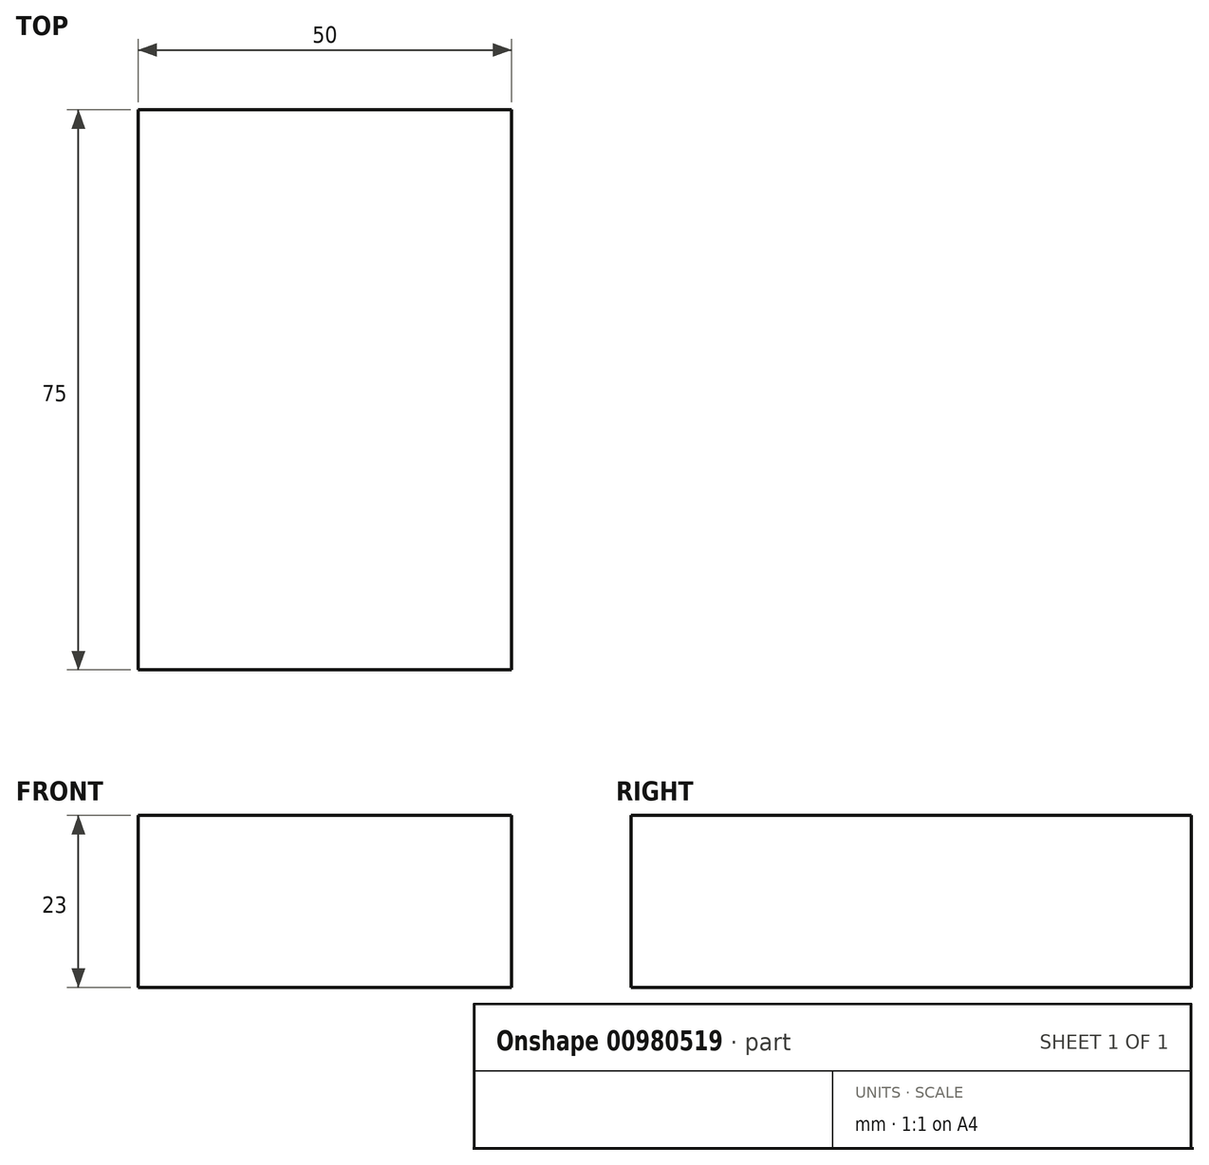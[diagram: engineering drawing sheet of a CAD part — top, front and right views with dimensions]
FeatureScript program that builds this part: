
annotation { "Feature Type Name" : "Feature", "Feature Type Description" : "" }
export const myFeature = defineFeature(function(context is Context, id is Id, definition is map)
    precondition{}
    {
        {
            var Q0;
            Q0=qCreatedBy(makeId("Top.planeOp"),FACE);
            var sketch = newSketch(context, id + "F0", { "sketchPlane" : qUnion([Q0])});
            skLineSegment(sketch, "E0.bottom", {"start": v(0, 0) * mm, "end": v(-50, 0) * mm});
            skLineSegment(sketch, "E0.top", {"start": v(0, 75) * mm, "end": v(-50, 75) * mm});
            skLineSegment(sketch, "E0.left", {"start": v(0, 0) * mm, "end": v(0, 75) * mm});
            skLineSegment(sketch, "E0.right", {"start": v(-50, 0) * mm, "end": v(-50, 75) * mm});
            skSolve(sketch);
        }
        {
            var Q0;
            Q0=makeQuery(id+"F0.imprint","IMPRINT",FACE,{"disambiguationData":[TD([[makeQuery(id+"F0.imprint","IMPRINT",EDGE,{"derivedFrom":sQuery(id+"F0.wireOp",EDGE,"E0.bottom")}),-1.0]])]});
            extrude(context, id + "F1", {"entities" : qUnion([Q0]), "depth" : 23 * mm, "offsetDistance" : 25.4 * mm});
        }
    });
